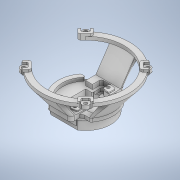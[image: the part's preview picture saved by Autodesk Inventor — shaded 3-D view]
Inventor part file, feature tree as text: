
AUTODESK INVENTOR PART (.ipt)
format: ipt  version: 2020 (Build 240168000, 168)  size: 1,348,096 bytes
history: native  units: mm
features: projected_geometry x49, sketch x28, extrude x21, other x9, fillet x8, chamfer x4, loft x2, revolve x1, pattern_circular x1, mirror x1
ambient origin geometry x8: Origin, YZ Plane, XZ Plane, XY Plane, X Axis, Y Axis, Z Axis, Center Point
bodies: Body1 (feature_tree)
feature tree (124):
  other  "Твердое тело1"
  extrude  "Выдавливание1"  Depth=17.1mm
  extrude  "Выдавливание2"  Depth=17.1mm
  other  "РабПлоскость1"
  sketch  "Эскиз3"
  other  "РабОсь1"
  revolve  "Вращение1"
  extrude  "Выдавливание3"  Depth=25.0mm
  extrude  "Выдавливание4"  Depth=5.3mm
  extrude  "Выдавливание5"  Depth=44.7mm
  extrude  "Выдавливание6"  Depth=7.7mm TaperAngle=0.0deg
  extrude  "Выдавливание7"  Depth=5.0mm
  extrude  "Выдавливание8"  Depth=30.65mm
  sketch  "Эскиз10"
  extrude  "Выдавливание9"  Depth=2.5mm TaperAngle=0.0deg
  fillet  "Сопряжение1"  Radius=0.2mm
  fillet  "Сопряжение2"  [1 undecoded]
  fillet  "Сопряжение3"  Radius=1.85mm
  extrude  "Выдавливание10"  Depth=30.0mm
  fillet  "Сопряжение4"  Radius=2.0mm
  fillet  "Сопряжение5"  Radius=3.0mm
  extrude  "камера"  Depth=38.0mm
  extrude  "труба"  Depth=10.0mm TaperAngle=0.0deg
  sketch  "Эскиз15"
  other  "РабПлоскость2"
  extrude  "Выдавливание12"  Depth=5.2mm
  extrude  "Выдавливание13"  Depth=6.0mm
  chamfer  "Фаска1"  Distance=29.46mm
  fillet  "Сопряжение6"  Radius=10.0mm
  fillet  "Сопряжение7"  Radius=9.5mm
  other  "РабОсь2"
  pattern_circular  "Круговой массив1"  [2 undecoded]
  extrude  "Выдавливание15"  TaperAngle=60.0deg  [1 undecoded]
  chamfer  "Фаска2"  Distance=6.0mm
  sketch  "Эскиз20"
  extrude  "Выдавливание16"  Depth=6.0mm
  fillet  "Сопряжение8"  Radius=14.2mm
  other  "РабПлоскость3"
  extrude  "Выдавливание17"  Depth=9.5mm
  extrude  "Выдавливание18"  Depth=2.0mm
  sketch  "Эскиз24"
  sketch  "Эскиз25"
  sketch  "Эскиз26"
  extrude  "Выдавливание19"  Depth=13.962634mm
  loft  "Лофт1"
  other  "РабПлоскость4"
  mirror  "Зеркальное отражение1"
  extrude  "Выдавливание20"  Depth=2.0mm TaperAngle=0.0deg
  loft  "Лофт2"
  extrude  "Выдавливание21"  Depth=6.0mm
  chamfer  "Фаска3"  Distance=6.0mm
  chamfer  "Фаска4"  Distance=1.7mm
  sketch  "Эскиз1"
  sketch  "Эскиз2"
  projected_geometry  "Спроецированная петля1"
  projected_geometry  "Спроецированная петля2"
  sketch  "Эскиз4"
  projected_geometry  "Спроецированная петля3"
  sketch  "Эскиз5"
  sketch  "Эскиз6"
  projected_geometry  "Спроецированная петля4"
  sketch  "Эскиз7"
  projected_geometry  "Спроецированная петля5"
  sketch  "Эскиз8"
  projected_geometry  "Спроецированная петля6"
  projected_geometry  "Спроецированная петля7"
  projected_geometry  "Спроецированная петля8"
  sketch  "Эскиз9"
  projected_geometry  "Спроецированная петля9"
  projected_geometry  "Спроецированная петля10"
  projected_geometry  "Спроецированная петля11"
  projected_geometry  "Спроецированная петля12"
  sketch  "Эскиз11"
  sketch  "Эскиз12"
  projected_geometry  "Спроецированная петля13"
  projected_geometry  "Спроецированная петля14"
  projected_geometry  "Спроецированная петля15"
  sketch  "Эскиз14"
  projected_geometry  "Спроецированная петля20"
  projected_geometry  "Спроецированная петля21"
  projected_geometry  "Спроецированная петля22"
  projected_geometry  "Спроецированная петля23"
  sketch  "Эскиз16"
  projected_geometry  "Спроецированная петля24"
  sketch  "Эскиз17"
  projected_geometry  "Спроецированная петля25"
  sketch  "Эскиз18"
  sketch  "Эскиз19"
  projected_geometry  "Спроецированная петля26"
  projected_geometry  "Спроецированная петля27"
  projected_geometry  "Спроецированная петля28"
  projected_geometry  "Спроецированная петля29"
  sketch  "Эскиз21"
  projected_geometry  "Спроецированная петля30"
  projected_geometry  "Спроецированная петля31"
  projected_geometry  "Спроецированная петля32"
  projected_geometry  "Спроецированная петля33"
  projected_geometry  "Спроецированная петля34"
  projected_geometry  "Спроецированная петля35"
  projected_geometry  "Спроецированная петля36"
  projected_geometry  "Спроецированная петля37"
  projected_geometry  "Спроецированная петля38"
  projected_geometry  "Спроецированная петля39"
  sketch  "Эскиз22"
  projected_geometry  "Спроецированная петля40"
  projected_geometry  "Спроецированная петля41"
  projected_geometry  "Спроецированная петля42"
  projected_geometry  "Спроецированная петля43"
  projected_geometry  "Спроецированная петля44"
  sketch  "Эскиз23"
  projected_geometry  "Спроецированная петля45"
  projected_geometry  "Спроецированная петля46"
  projected_geometry  "Спроецированная петля47"
  projected_geometry  "Спроецированная петля48"
  projected_geometry  "Спроецированная петля49"
  projected_geometry  "Спроецированная петля50"
  other  "Ребра1"
  sketch  "Эскиз27"
  projected_geometry  "Спроецированная петля51"
  sketch  "Эскиз28"
  projected_geometry  "Спроецированная петля52"
  projected_geometry  "Спроецированная петля53"
  other  "Ребра2"
  sketch  "Эскиз31"
note: 4 required parameter values undecoded (feature->parameter linkage not recoverable at this tier; creation-order binding heuristic only, values carry confidence <= 0.55)
